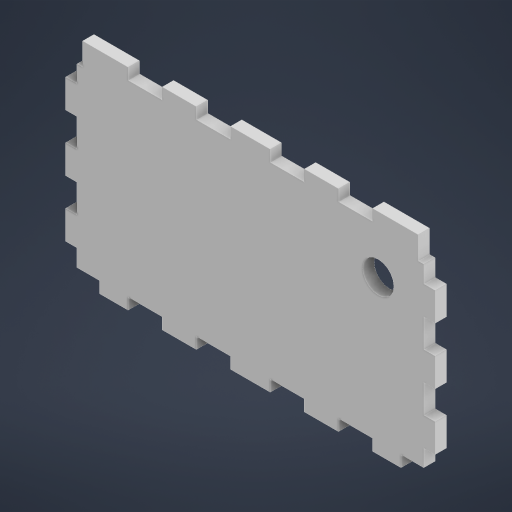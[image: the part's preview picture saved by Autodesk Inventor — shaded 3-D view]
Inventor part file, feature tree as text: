
AUTODESK INVENTOR PART (.ipt)
format: ipt  version: 2023.2 (Build 272271000, 271)  size: 373,248 bytes
history: native  units: mm
features: sketch x3
ambient origin geometry x8: Origin, YZ Plane, XZ Plane, XY Plane, X Axis, Y Axis, Z Axis, Center Point
bodies: Body1 (feature_tree)
feature tree (3):
  sketch  "Sketch1"  dims[d228=130.0mm]
  sketch  "Sketch2"  dims[d229=74.0mm]
  sketch  "Sketch3"  dims[d230=4.0mm d231=0.0mm d234=10.0mm d235=12.0mm d236=12.0mm d237=12.0mm d238=14.0mm d240=12.0mm d242=12.0mm d243=10.0mm d244=12.0mm d245=12.0mm d246=12.0mm d249=10.0mm d251=10.0mm d255=10.0mm d259=4.0mm d260=0.0mm d262=4.0mm d267=10.0mm d268=10.0mm d271=10.0mm d272=14.0mm d274=6.0mm d278=8.0mm d279=11.0mm d280=20.0mm d281=20.0mm d282=4.0mm d283=0.0mm d9=0.5mm d10=0.872665mm d11=0.5mm d12=0.872665mm d13=0.5mm d14=0.872665mm d27=0.5mm d28=0.872665mm d29=0.5mm d30=0.872665mm d88=0.5mm d89=0.872665mm d90=0.5mm d91=0.872665mm d116=0.5mm d117=0.872665mm d118=0.5mm d119=0.872665mm d154=0.5mm d155=0.872665mm d156=0.5mm d157=0.872665mm d181=0.5mm d182=0.872665mm d183=0.5mm d184=0.872665mm d221=0.5mm d222=0.872665mm d223=0.5mm d224=0.872665mm]
